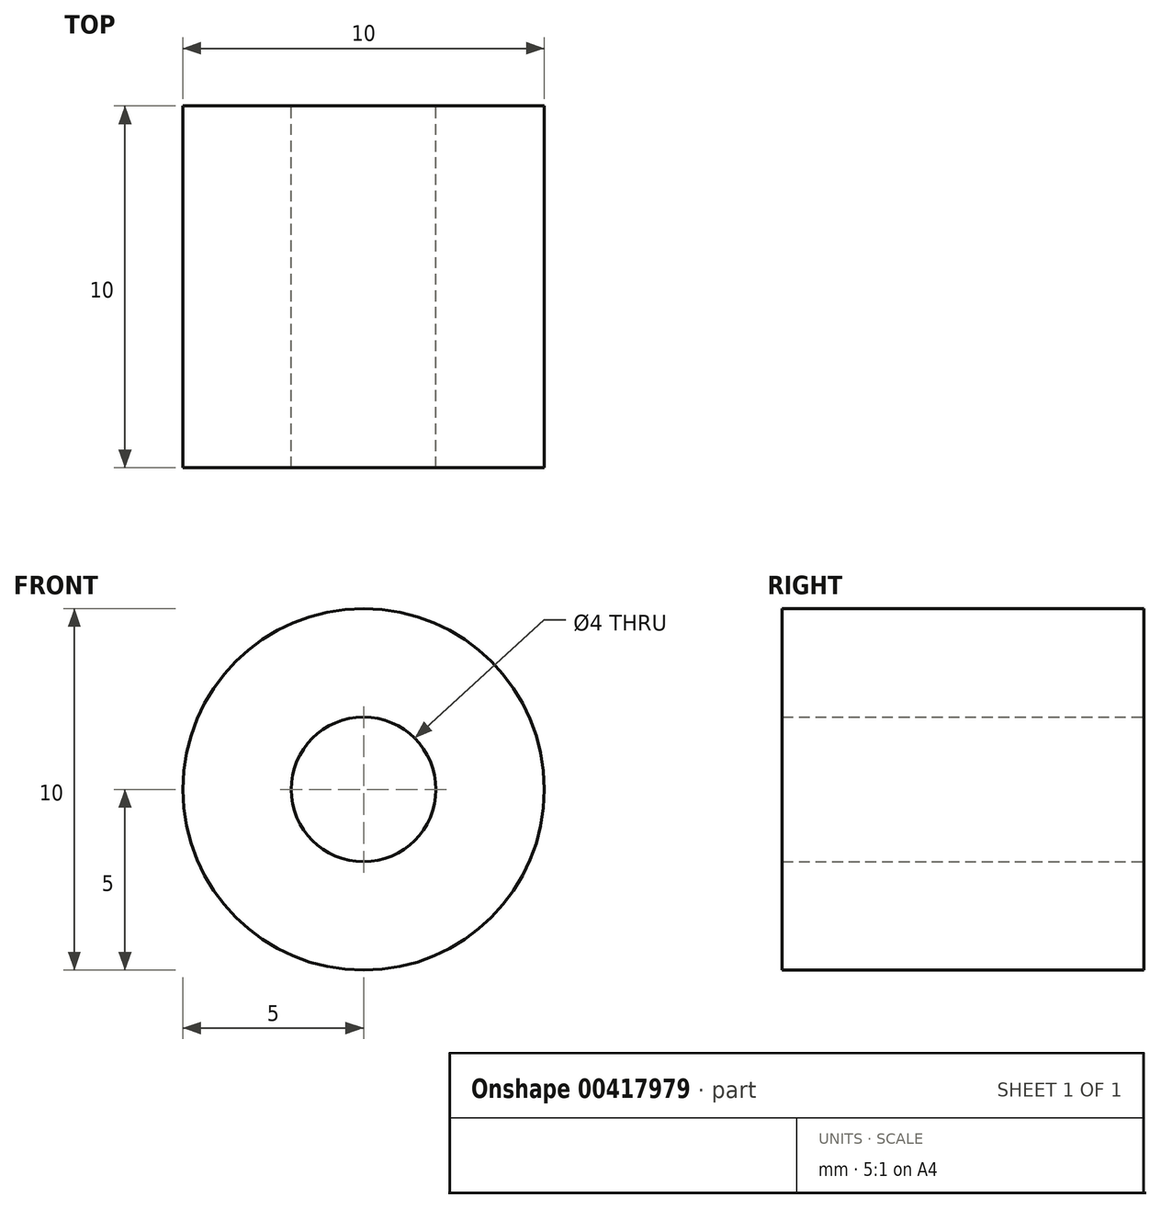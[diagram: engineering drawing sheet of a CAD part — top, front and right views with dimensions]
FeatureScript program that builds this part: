
annotation { "Feature Type Name" : "Feature", "Feature Type Description" : "" }
export const myFeature = defineFeature(function(context is Context, id is Id, definition is map)
    precondition{}
    {
        {
            var Q0;
            Q0=qCreatedBy(makeId("Front.planeOp"),FACE);
            var sketch = newSketch(context, id + "F0", { "sketchPlane" : qUnion([Q0])});
            skCircle(sketch, "E0", {"center": v(0, 0) * mm, "radius": 2 * mm});
            skCircle(sketch, "E1", {"center": v(0, 0) * mm, "radius": 5 * mm});
            skSolve(sketch);
        }
        {
            var Q0;
            Q0 = qSketchRegion(id + "F0", true);
            extrude(context, id + "F1", {"entities" : qUnion([Q0]), "depth" : 10 * mm});
        }
    });
